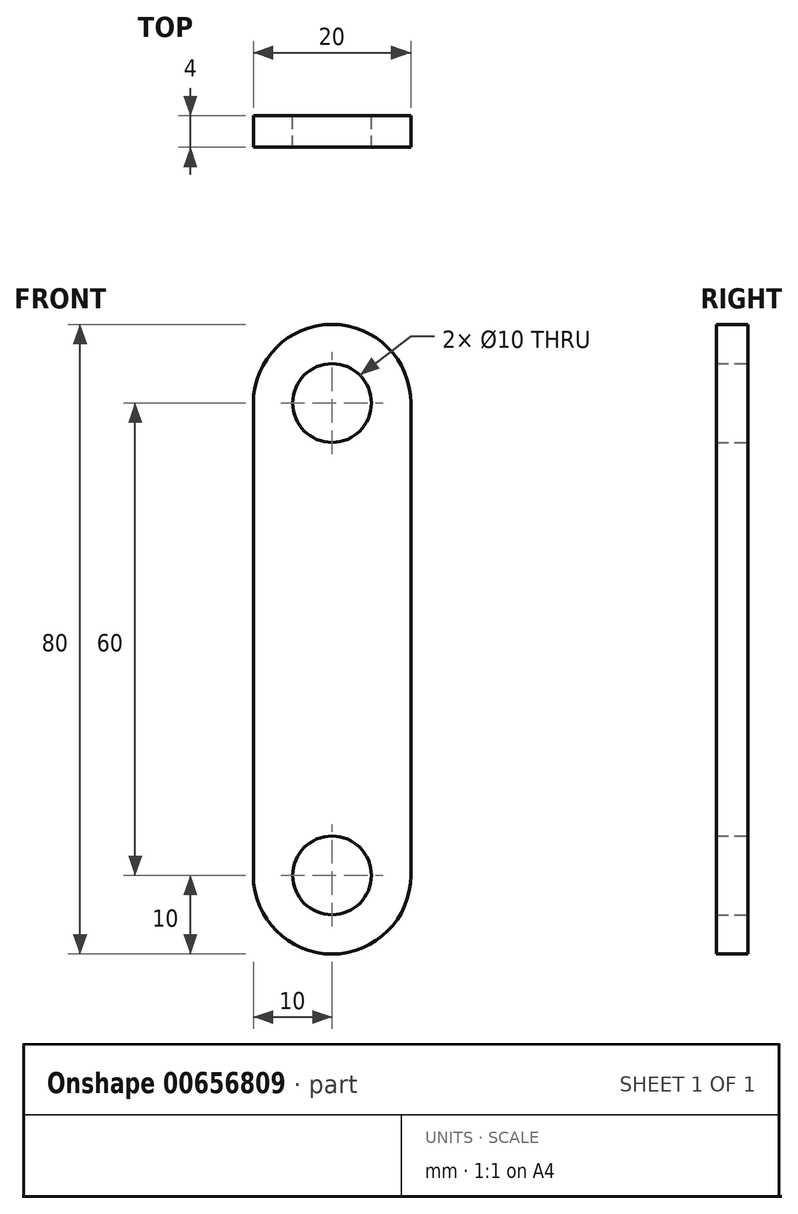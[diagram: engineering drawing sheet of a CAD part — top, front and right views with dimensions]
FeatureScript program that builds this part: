
annotation { "Feature Type Name" : "Feature", "Feature Type Description" : "" }
export const myFeature = defineFeature(function(context is Context, id is Id, definition is map)
    precondition{}
    {
        {
            var Q0;
            Q0=qCreatedBy(makeId("Front.planeOp"),FACE);
            var sketch = newSketch(context, id + "F0", { "sketchPlane" : qUnion([Q0])});
            skCircle(sketch, "E0", {"center": v(0, 0) * mm, "radius": 5 * mm});
            skLineSegment(sketch, "E1", {"start": v(0, 0) * mm, "end": v(0, -60) * mm, "construction": true});
            skCircle(sketch, "E2", {"center": v(0, -60) * mm, "radius": 5 * mm});
            skCircle(sketch, "E3", {"center": v(0, 0) * mm, "radius": 10 * mm});
            skCircle(sketch, "E4", {"center": v(0, -60) * mm, "radius": 10 * mm});
            skLineSegment(sketch, "E5", {"start": v(0, 0) * mm, "end": v(10, 0) * mm, "construction": true});
            skLineSegment(sketch, "E6", {"start": v(10, 0) * mm, "end": v(10, -60) * mm});
            skLineSegment(sketch, "E7.MirrorCS", {"start": v(-10, 0) * mm, "end": v(-10, -60) * mm});
            skSolve(sketch);
        }
        {
            var Q0;
            Q0=makeQuery(id+"F0.imprint","IMPRINT",FACE,{"disambiguationData":[TD([[makeQuery(id+"F0.imprint","IMPRINT",EDGE,{"derivedFrom":sQuery(id+"F0.wireOp",EDGE,"E0")}),-1.0]])]});
            var Q1;
            {var subQ0=sQuery(id+"F0.wireOp",EDGE,"E6");Q1=makeQuery(id+"F0.imprint","IMPRINT",FACE,{"disambiguationData":[TD([[makeQuery(id+"F0.imprint","IMPRINT",EDGE,{"derivedFrom":subQ0}),-1.0]])]});}
            var Q2;
            Q2=makeQuery(id+"F0.imprint","IMPRINT",FACE,{"disambiguationData":[TD([[makeQuery(id+"F0.imprint","IMPRINT",EDGE,{"derivedFrom":sQuery(id+"F0.wireOp",EDGE,"E2")}),-1.0]])]});
            extrude(context, id + "F1", {"entities" : qUnion([Q0, Q1, Q2]), "depth" : 4 * mm, "offsetDistance" : 25 * mm});
        }
    });
